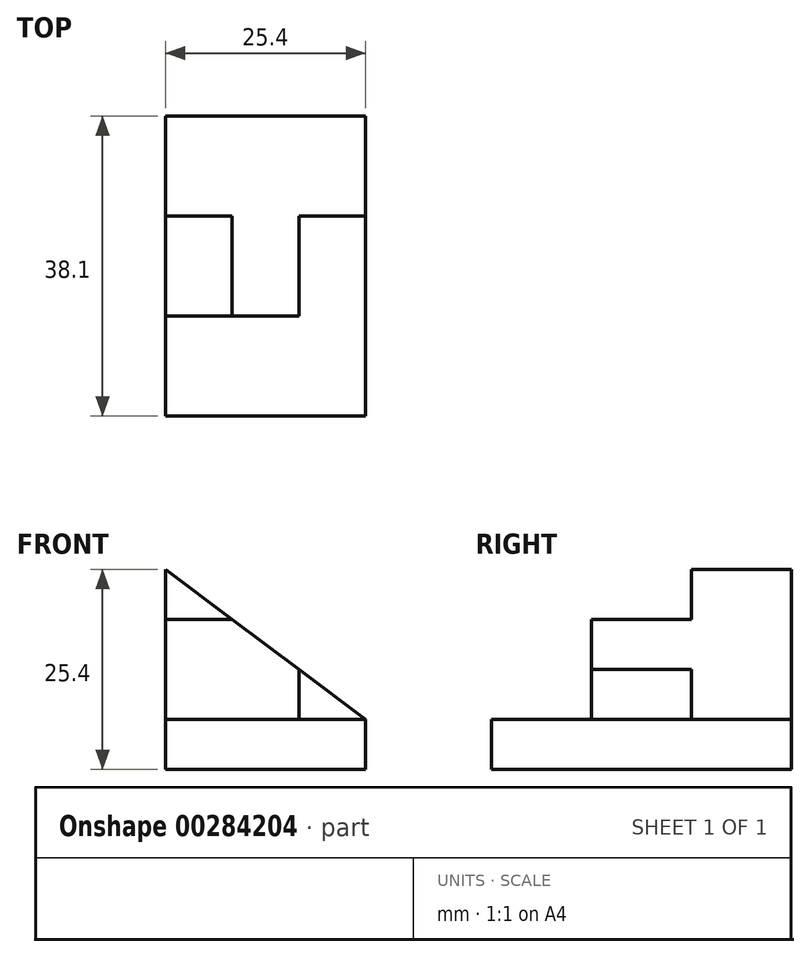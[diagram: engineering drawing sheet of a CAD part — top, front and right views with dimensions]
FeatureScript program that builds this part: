
annotation { "Feature Type Name" : "Feature", "Feature Type Description" : "" }
export const myFeature = defineFeature(function(context is Context, id is Id, definition is map)
    precondition{}
    {
        {
            var Q0;
            Q0=qCreatedBy(makeId("Front.planeOp"),FACE);
            var sketch = newSketch(context, id + "F0", { "sketchPlane" : qUnion([Q0])});
            skLineSegment(sketch, "E0", {"start": v(0, 0) * mm, "end": v(25.4, 0) * mm});
            skLineSegment(sketch, "E1", {"start": v(25.4, 0) * mm, "end": v(25.4, 6.35) * mm});
            skLineSegment(sketch, "E2", {"start": v(25.4, 6.35) * mm, "end": v(0, 6.35) * mm});
            skLineSegment(sketch, "E3", {"start": v(0, 6.35) * mm, "end": v(0, 0) * mm});
            skSolve(sketch);
        }
        {
            var Q0;
            Q0 = qSketchRegion(id + "F0", true);
            extrude(context, id + "F1", {"entities" : qUnion([Q0]), "oppositeDirection" : true, "depth" : 38.1 * mm});
        }
        {
            var Q0;
            Q0=makeQuery(id+"F1.opExtrude","SWEPT_FACE",FACE,{"disambiguationData":[OSD([sQuery(id+"F0.wireOp",EDGE,"E1")])]});
            var sketch = newSketch(context, id + "F2", { "sketchPlane" : qUnion([Q0])});
            skLineSegment(sketch, "E4", {"start": v(12.7, 6.35) * mm, "end": v(12.7, 19.05) * mm});
            skLineSegment(sketch, "E5", {"start": v(12.7, 19.05) * mm, "end": v(25.4, 19.05) * mm});
            skLineSegment(sketch, "E6", {"start": v(25.4, 19.05) * mm, "end": v(25.4, 25.4) * mm});
            skLineSegment(sketch, "E7", {"start": v(12.7, 6.35) * mm, "end": v(38.1, 6.35) * mm});
            skLineSegment(sketch, "E8", {"start": v(38.1, 6.35) * mm, "end": v(38.1, 25.4) * mm});
            skLineSegment(sketch, "E9", {"start": v(38.1, 25.4) * mm, "end": v(25.4, 25.4) * mm});
            skSolve(sketch);
        }
        {
            var Q0;
            Q0=makeQuery(id+"F2.imprint","IMPRINT",FACE,{"disambiguationData":[TD([[makeQuery(id+"F2.imprint","IMPRINT",EDGE,{"derivedFrom":sQuery(id+"F2.wireOp",EDGE,"E4")}),-1.0]])]});
            extrude(context, id + "F3", {"entities" : qUnion([Q0]), "operationType" : NewBodyOperationType.ADD, "oppositeDirection" : true, "depth" : 25.4 * mm});
        }
        {
            var Q0;
            Q0=makeQuery(id+"F3.boolean.opBoolean","MERGE",FACE,{"derivedFrom":[makeQuery(id+"F1.opExtrude","CAP_FACE",FACE,{"disambiguationData":[OSD([sQuery(id+"F0.wireOp",EDGE,"E0"),sQuery(id+"F0.wireOp",EDGE,"E1"),sQuery(id+"F0.wireOp",EDGE,"E2"),sQuery(id+"F0.wireOp",EDGE,"E3")])],"isStart":false}),makeQuery(id+"F3.opExtrude","SWEPT_FACE",FACE,{"disambiguationData":[OSD([sQuery(id+"F2.wireOp",EDGE,"E8")])]})]});
            var sketch = newSketch(context, id + "F4", { "sketchPlane" : qUnion([Q0])});
            skLineSegment(sketch, "E10", {"start": v(-25.4, 6.35) * mm, "end": v(0, 25.4) * mm});
            skLineSegment(sketch, "E11", {"start": v(0, 25.4) * mm, "end": v(-25.4, 25.4) * mm});
            skLineSegment(sketch, "E12", {"start": v(-25.4, 25.4) * mm, "end": v(-25.4, 6.35) * mm});
            skSolve(sketch);
        }
        {
            var Q0;
            Q0 = qSketchRegion(id + "F4", true);
            extrude(context, id + "F5", {"entities" : qUnion([Q0]), "operationType" : NewBodyOperationType.REMOVE, "endBound" : BoundingType.THROUGH_ALL, "oppositeDirection" : true, "depth" : 25.4 * mm});
        }
        {
            var Q0;
            Q0=makeQuery(id+"F3.opExtrude","SWEPT_FACE",FACE,{"disambiguationData":[OSD([sQuery(id+"F2.wireOp",EDGE,"E4")])]});
            var sketch = newSketch(context, id + "F6", { "sketchPlane" : qUnion([Q0])});
            skLineSegment(sketch, "E13", {"start": v(16.93, 12.7) * mm, "end": v(16.93, 6.35) * mm});
            skLineSegment(sketch, "E14", {"start": v(16.93, 6.35) * mm, "end": v(25.4, 6.35) * mm});
            skLineSegment(sketch, "E15", {"start": v(25.4, 6.35) * mm, "end": v(16.93, 12.7) * mm});
            skSolve(sketch);
        }
        {
            var Q0;
            Q0 = qSketchRegion(id + "F6", true);
            extrude(context, id + "F7", {"entities" : qUnion([Q0]), "operationType" : NewBodyOperationType.REMOVE, "oppositeDirection" : true, "depth" : 12.7 * mm});
        }
    });
